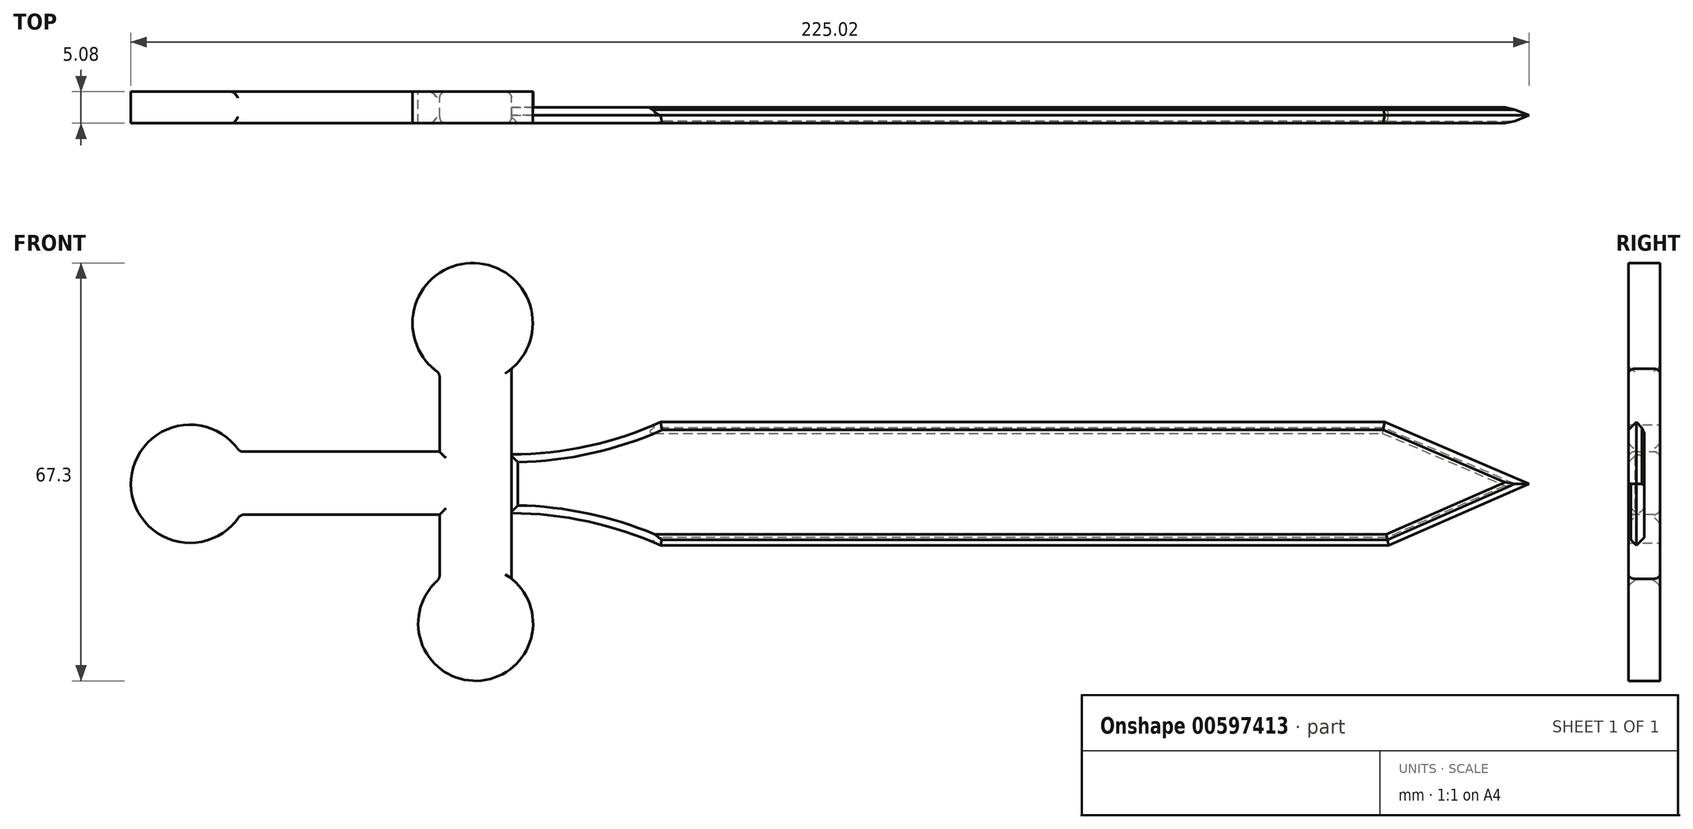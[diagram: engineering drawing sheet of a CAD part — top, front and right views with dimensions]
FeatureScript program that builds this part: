
annotation { "Feature Type Name" : "Feature", "Feature Type Description" : "" }
export const myFeature = defineFeature(function(context is Context, id is Id, definition is map)
    precondition{}
    {
        {
            var Q0;
            Q0=qCreatedBy(makeId("Front.planeOp"),FACE);
            var sketch = newSketch(context, id + "F0", { "sketchPlane" : qUnion([Q0])});
            skLineSegment(sketch, "E0.bottom", {"start": v(-78.76, 5.18) * mm, "end": v(-27.96, 5.18) * mm});
            skLineSegment(sketch, "E0.top", {"start": v(-78.76, -4.98) * mm, "end": v(-27.96, -4.98) * mm});
            skLineSegment(sketch, "E0.left", {"start": v(-78.76, 5.18) * mm, "end": v(-78.76, -4.98) * mm});
            skLineSegment(sketch, "E0.right", {"start": v(-27.96, 5.18) * mm, "end": v(-27.96, -4.98) * mm});
            skCircle(sketch, "E1", {"center": v(-75.72, 0) * mm, "radius": 9.52 * mm});
            skLineSegment(sketch, "E2.bottom", {"start": v(-35.56, 22.01) * mm, "end": v(-23.95, 22.01) * mm});
            skLineSegment(sketch, "E2.top", {"start": v(-35.56, -22.5) * mm, "end": v(-23.95, -22.5) * mm});
            skLineSegment(sketch, "E2.left", {"start": v(-35.56, 22.01) * mm, "end": v(-35.56, -22.5) * mm});
            skLineSegment(sketch, "E2.right", {"start": v(-23.95, 22.01) * mm, "end": v(-23.95, -22.5) * mm});
            skCircle(sketch, "E3", {"center": v(-30.24, 25.88) * mm, "radius": 9.68 * mm});
            skCircle(sketch, "E4", {"center": v(-29.75, -22.5) * mm, "radius": 9.24 * mm});
            skSolve(sketch);
        }
        {
            var Q0;
            Q0 = qSketchRegion(id + "F0", true);
            extrude(context, id + "F1", {"entities" : qUnion([Q0]), "endBound" : BoundingType.SYMMETRIC, "depth" : 5.08 * mm, "offsetDistance" : 25.4 * mm});
        }
        {
            var Q0;
            {var subQ0=sQuery(id+"F0.wireOp",EDGE,"E0.top");Q0=makeQuery(id+"F1.opExtrude","CAP_EDGE",EDGE,{"disambiguationData":[OSD([subQ0]),TDD([makeQuery(id+"F0.imprint","IMPRINT",EDGE,{"disambiguationData":[TD([[makeQuery(id+"F0.imprint","INTERSECT",VERTEX,{"derivedFrom":[subQ0,sQuery(id+"F0.wireOp",EDGE,"E1")]}),-1.0]])],"derivedFrom":subQ0})])],"isStart":false});}
            var Q1;
            {var subQ0=sQuery(id+"F0.wireOp",EDGE,"E0.bottom");Q1=makeQuery(id+"F1.opExtrude","CAP_EDGE",EDGE,{"disambiguationData":[OSD([subQ0]),TDD([makeQuery(id+"F0.imprint","IMPRINT",EDGE,{"disambiguationData":[TD([[makeQuery(id+"F0.imprint","INTERSECT",VERTEX,{"derivedFrom":[subQ0,sQuery(id+"F0.wireOp",EDGE,"E1")]}),-1.0]])],"derivedFrom":subQ0})])],"isStart":false});}
            var Q2;
            Q2=makeQuery(id+"F1.opExtrude","SWEPT_EDGE",EDGE,{"disambiguationData":[OSD([sQuery(id+"F0.wireOp",EDGE,"E0.top"),sQuery(id+"F0.wireOp",EDGE,"E1")])]});
            var Q3;
            Q3=makeQuery(id+"F1.opExtrude","SWEPT_EDGE",EDGE,{"disambiguationData":[OSD([sQuery(id+"F0.wireOp",EDGE,"E0.bottom"),sQuery(id+"F0.wireOp",EDGE,"E1")])]});
            var Q4;
            {var subQ0=sQuery(id+"F0.wireOp",EDGE,"E2.left");Q4=makeQuery(id+"F1.opExtrude","CAP_EDGE",EDGE,{"disambiguationData":[OSD([subQ0]),TDD([makeQuery(id+"F0.imprint","IMPRINT",EDGE,{"disambiguationData":[TD([[makeQuery(id+"F0.imprint","INTERSECT",VERTEX,{"derivedFrom":[sQuery(id+"F0.wireOp",EDGE,"E0.bottom"),subQ0]}),1.0]])],"derivedFrom":subQ0})])],"isStart":false});}
            var Q5;
            {var subQ0=sQuery(id+"F0.wireOp",EDGE,"E2.right");Q5=makeQuery(id+"F1.opExtrude","CAP_EDGE",EDGE,{"disambiguationData":[OSD([subQ0]),TDD([makeQuery(id+"F0.imprint","IMPRINT",EDGE,{"disambiguationData":[TD([[makeQuery(id+"F0.imprint","INTERSECT",VERTEX,{"derivedFrom":[sQuery(id+"F0.wireOp",EDGE,"E0.top"),subQ0]}),-1.0]])],"derivedFrom":subQ0})])],"isStart":false});}
            var Q6;
            {var subQ0=sQuery(id+"F0.wireOp",EDGE,"E2.right");Q6=makeQuery(id+"F1.opExtrude","CAP_EDGE",EDGE,{"disambiguationData":[OSD([subQ0]),TDD([makeQuery(id+"F0.imprint","IMPRINT",EDGE,{"disambiguationData":[TD([[makeQuery(id+"F0.imprint","INTERSECT",VERTEX,{"derivedFrom":[sQuery(id+"F0.wireOp",EDGE,"E0.bottom"),subQ0]}),1.0]])],"derivedFrom":subQ0})])],"isStart":false});}
            var Q7;
            {var subQ0=sQuery(id+"F0.wireOp",EDGE,"E2.left");Q7=makeQuery(id+"F1.opExtrude","CAP_EDGE",EDGE,{"disambiguationData":[OSD([subQ0]),TDD([makeQuery(id+"F0.imprint","IMPRINT",EDGE,{"disambiguationData":[TD([[makeQuery(id+"F0.imprint","INTERSECT",VERTEX,{"derivedFrom":[sQuery(id+"F0.wireOp",EDGE,"E0.top"),subQ0]}),-1.0]])],"derivedFrom":subQ0})])],"isStart":false});}
            var Q8;
            Q8=makeQuery(id+"F1.opExtrude","SWEPT_EDGE",EDGE,{"disambiguationData":[OSD([sQuery(id+"F0.wireOp",EDGE,"E2.left"),sQuery(id+"F0.wireOp",EDGE,"E3")])]});
            var Q9;
            Q9=makeQuery(id+"F1.opExtrude","SWEPT_EDGE",EDGE,{"disambiguationData":[OSD([sQuery(id+"F0.wireOp",EDGE,"E2.left"),sQuery(id+"F0.wireOp",EDGE,"E4")])]});
            var Q10;
            Q10=makeQuery(id+"F1.opExtrude","CAP_EDGE",EDGE,{"disambiguationData":[OSD([sQuery(id+"F0.wireOp",EDGE,"E0.bottom")])],"isStart":true});
            var Q11;
            Q11=makeQuery(id+"F1.opExtrude","CAP_EDGE",EDGE,{"disambiguationData":[OSD([sQuery(id+"F0.wireOp",EDGE,"E0.top")])],"isStart":true});
            var Q12;
            {var subQ0=sQuery(id+"F0.wireOp",EDGE,"E2.left");Q12=makeQuery(id+"F1.opExtrude","CAP_EDGE",EDGE,{"disambiguationData":[OSD([subQ0]),TDD([makeQuery(id+"F0.imprint","IMPRINT",EDGE,{"disambiguationData":[TD([[makeQuery(id+"F0.imprint","INTERSECT",VERTEX,{"derivedFrom":[sQuery(id+"F0.wireOp",EDGE,"E0.top"),subQ0]}),-1.0]])],"derivedFrom":subQ0})])],"isStart":true});}
            var Q13;
            {var subQ0=sQuery(id+"F0.wireOp",EDGE,"E2.right");Q13=makeQuery(id+"F1.opExtrude","CAP_EDGE",EDGE,{"disambiguationData":[OSD([subQ0]),TDD([makeQuery(id+"F0.imprint","IMPRINT",EDGE,{"disambiguationData":[TD([[makeQuery(id+"F0.imprint","INTERSECT",VERTEX,{"derivedFrom":[subQ0,sQuery(id+"F0.wireOp",EDGE,"CYwJg3hl-RuJJ-tjd6-eNec-YJv9DW7DHuWa")]}),-1.0]])],"derivedFrom":subQ0})])],"isStart":true});}
            var Q14;
            {var subQ0=sQuery(id+"F0.wireOp",EDGE,"E2.right");Q14=makeQuery(id+"F1.opExtrude","CAP_EDGE",EDGE,{"disambiguationData":[OSD([subQ0]),TDD([makeQuery(id+"F0.imprint","IMPRINT",EDGE,{"disambiguationData":[TD([[makeQuery(id+"F0.imprint","INTERSECT",VERTEX,{"derivedFrom":[subQ0,sQuery(id+"F0.wireOp",EDGE,"E3")]}),-1.0]])],"derivedFrom":subQ0})])],"isStart":true});}
            var Q15;
            {var subQ0=sQuery(id+"F0.wireOp",EDGE,"E2.left");Q15=makeQuery(id+"F1.opExtrude","CAP_EDGE",EDGE,{"disambiguationData":[OSD([subQ0]),TDD([makeQuery(id+"F0.imprint","IMPRINT",EDGE,{"disambiguationData":[TD([[makeQuery(id+"F0.imprint","INTERSECT",VERTEX,{"derivedFrom":[sQuery(id+"F0.wireOp",EDGE,"E0.bottom"),subQ0]}),1.0]])],"derivedFrom":subQ0})])],"isStart":true});}
            fillet(context, id + "F2", {"entities" : qUnion([Q0, Q1, Q2, Q3, Q4, Q5, Q6, Q7, Q8, Q9, Q10, Q11, Q12, Q13, Q14, Q15]), "radius" : 1.02 * mm, "tangentPropagation" : true, "allowEdgeOverflow" : false});
        }
        {
            var Q0;
            Q0=qCreatedBy(makeId("Front.planeOp"),FACE);
            var sketch = newSketch(context, id + "F3", { "sketchPlane" : qUnion([Q0])});
            skLineSegment(sketch, "E5", {"start": v(-24.21, 4.73) * mm, "end": v(-24.21, -4.73) * mm});
            skLineSegment(sketch, "E6", {"start": v(0, 9.92) * mm, "end": v(0, -9.92) * mm});
            skLineSegment(sketch, "E7.bottom", {"start": v(-24.21, 4.73) * mm, "end": v(0, 4.73) * mm});
            skLineSegment(sketch, "E7.top", {"start": v(-24.21, -4.73) * mm, "end": v(0, -4.73) * mm});
            skLineSegment(sketch, "E7.right", {"start": v(0, 4.73) * mm, "end": v(0, -4.73) * mm});
            skArc(sketch, "E8", {"start": v(-24.21, 4.73) * mm, "mid": v(-11.83, 6.05) * mm, "end": v(0, 9.92) * mm});
            skArc(sketch, "E9", {"start": v(0, -9.92) * mm, "mid": v(-11.83, -6.05) * mm, "end": v(-24.21, -4.73) * mm});
            skLineSegment(sketch, "E10", {"start": v(0, 9.92) * mm, "end": v(116.57, 9.92) * mm});
            skLineSegment(sketch, "E11", {"start": v(0, -9.92) * mm, "end": v(117.18, -9.92) * mm});
            skLineSegment(sketch, "E12", {"start": v(116.57, 9.92) * mm, "end": v(139.78, 0) * mm});
            skLineSegment(sketch, "E13", {"start": v(139.78, 0) * mm, "end": v(117.18, -9.92) * mm});
            skLineSegment(sketch, "E14", {"start": v(-24.21, -4.73) * mm, "end": v(-24.21, 4.73) * mm});
            skSolve(sketch);
        }
        {
            var Q0;
            Q0 = qSketchRegion(id + "F3", true);
            extrude(context, id + "F4", {"entities" : qUnion([Q0]), "operationType" : NewBodyOperationType.ADD, "depth" : 2.54 * mm, "offsetDistance" : 25.4 * mm});
        }
        {
            var Q0;
            Q0=makeQuery(id+"F4.opExtrude","CAP_FACE",FACE,{"disambiguationData":[OSD([sQuery(id+"F3.wireOp",EDGE,"E8"),sQuery(id+"F3.wireOp",EDGE,"E9"),sQuery(id+"F3.wireOp",EDGE,"E10"),sQuery(id+"F3.wireOp",EDGE,"E11"),sQuery(id+"F3.wireOp",EDGE,"E12"),sQuery(id+"F3.wireOp",EDGE,"E13"),sQuery(id+"F3.wireOp",EDGE,"E14")])],"isStart":false});
            var Q1;
            Q1=makeQuery(id+"F4.opExtrude","CAP_EDGE",EDGE,{"disambiguationData":[OSD([sQuery(id+"F3.wireOp",EDGE,"E10")])],"isStart":true});
            var Q2;
            Q2=makeQuery(id+"F4.opExtrude","CAP_EDGE",EDGE,{"disambiguationData":[OSD([sQuery(id+"F3.wireOp",EDGE,"E12")])],"isStart":true});
            chamfer(context, id + "F5", {"entities" : qUnion([Q0, Q1, Q2]), "width" : 1.27 * mm, "tangentPropagation" : true});
        }
        {
            var Q0;
            {var subQ0=sQuery(id+"F3.wireOp",EDGE,"E10");Q0=makeQuery(id+"F5.opChamfer","BLEND_EDGE",EDGE,{"blendedFrom":[makeQuery(id+"F4.opExtrude","CAP_EDGE",EDGE,{"disambiguationData":[OSD([subQ0])],"isStart":true}),makeQuery(id+"F4.opExtrude","CAP_FACE",FACE,{"disambiguationData":[OSD([sQuery(id+"F3.wireOp",EDGE,"E8"),sQuery(id+"F3.wireOp",EDGE,"E9"),subQ0,sQuery(id+"F3.wireOp",EDGE,"E11"),sQuery(id+"F3.wireOp",EDGE,"E12"),sQuery(id+"F3.wireOp",EDGE,"E13"),sQuery(id+"F3.wireOp",EDGE,"E14")])],"isStart":true})],"blendedInto":[makeQuery(id+"F4.opExtrude","CAP_FACE",FACE,{"disambiguationData":[OSD([sQuery(id+"F3.wireOp",EDGE,"E8"),sQuery(id+"F3.wireOp",EDGE,"E9"),subQ0,sQuery(id+"F3.wireOp",EDGE,"E11"),sQuery(id+"F3.wireOp",EDGE,"E12"),sQuery(id+"F3.wireOp",EDGE,"E13"),sQuery(id+"F3.wireOp",EDGE,"E14")])],"isStart":true})]});}
            var Q1;
            {var subQ0=sQuery(id+"F3.wireOp",EDGE,"E12");Q1=makeQuery(id+"F5.opChamfer","BLEND_EDGE",EDGE,{"blendedFrom":[makeQuery(id+"F4.opExtrude","CAP_EDGE",EDGE,{"disambiguationData":[OSD([subQ0])],"isStart":true}),makeQuery(id+"F4.opExtrude","CAP_FACE",FACE,{"disambiguationData":[OSD([sQuery(id+"F3.wireOp",EDGE,"E8"),sQuery(id+"F3.wireOp",EDGE,"E9"),sQuery(id+"F3.wireOp",EDGE,"E10"),sQuery(id+"F3.wireOp",EDGE,"E11"),subQ0,sQuery(id+"F3.wireOp",EDGE,"E13"),sQuery(id+"F3.wireOp",EDGE,"E14")])],"isStart":true})],"blendedInto":[makeQuery(id+"F4.opExtrude","CAP_FACE",FACE,{"disambiguationData":[OSD([sQuery(id+"F3.wireOp",EDGE,"E8"),sQuery(id+"F3.wireOp",EDGE,"E9"),sQuery(id+"F3.wireOp",EDGE,"E10"),sQuery(id+"F3.wireOp",EDGE,"E11"),subQ0,sQuery(id+"F3.wireOp",EDGE,"E13"),sQuery(id+"F3.wireOp",EDGE,"E14")])],"isStart":true})]});}
            var Q2;
            Q2=makeQuery(id+"F4.opExtrude","CAP_EDGE",EDGE,{"disambiguationData":[OSD([sQuery(id+"F3.wireOp",EDGE,"E13")])],"isStart":true});
            var Q3;
            Q3=makeQuery(id+"F4.opExtrude","CAP_EDGE",EDGE,{"disambiguationData":[OSD([sQuery(id+"F3.wireOp",EDGE,"E11")])],"isStart":true});
            var Q4;
            {var subQ0=sQuery(id+"F3.wireOp",EDGE,"E11");Q4=makeQuery(id+"F5.opChamfer","BLEND_EDGE",EDGE,{"blendedFrom":[makeQuery(id+"F4.opExtrude","CAP_EDGE",EDGE,{"disambiguationData":[OSD([subQ0])],"isStart":false}),makeQuery(id+"F4.opExtrude","CAP_FACE",FACE,{"disambiguationData":[OSD([sQuery(id+"F3.wireOp",EDGE,"E8"),sQuery(id+"F3.wireOp",EDGE,"E9"),sQuery(id+"F3.wireOp",EDGE,"E10"),subQ0,sQuery(id+"F3.wireOp",EDGE,"E12"),sQuery(id+"F3.wireOp",EDGE,"E13"),sQuery(id+"F3.wireOp",EDGE,"E14")])],"isStart":false})],"blendedInto":[makeQuery(id+"F4.opExtrude","CAP_FACE",FACE,{"disambiguationData":[OSD([sQuery(id+"F3.wireOp",EDGE,"E8"),sQuery(id+"F3.wireOp",EDGE,"E9"),sQuery(id+"F3.wireOp",EDGE,"E10"),subQ0,sQuery(id+"F3.wireOp",EDGE,"E12"),sQuery(id+"F3.wireOp",EDGE,"E13"),sQuery(id+"F3.wireOp",EDGE,"E14")])],"isStart":false})]});}
            var Q5;
            {var subQ0=sQuery(id+"F3.wireOp",EDGE,"E13");Q5=makeQuery(id+"F5.opChamfer","BLEND_EDGE",EDGE,{"blendedFrom":[makeQuery(id+"F4.opExtrude","CAP_EDGE",EDGE,{"disambiguationData":[OSD([subQ0])],"isStart":false}),makeQuery(id+"F4.opExtrude","CAP_FACE",FACE,{"disambiguationData":[OSD([sQuery(id+"F3.wireOp",EDGE,"E8"),sQuery(id+"F3.wireOp",EDGE,"E9"),sQuery(id+"F3.wireOp",EDGE,"E10"),sQuery(id+"F3.wireOp",EDGE,"E11"),sQuery(id+"F3.wireOp",EDGE,"E12"),subQ0,sQuery(id+"F3.wireOp",EDGE,"E14")])],"isStart":false})],"blendedInto":[makeQuery(id+"F4.opExtrude","CAP_FACE",FACE,{"disambiguationData":[OSD([sQuery(id+"F3.wireOp",EDGE,"E8"),sQuery(id+"F3.wireOp",EDGE,"E9"),sQuery(id+"F3.wireOp",EDGE,"E10"),sQuery(id+"F3.wireOp",EDGE,"E11"),sQuery(id+"F3.wireOp",EDGE,"E12"),subQ0,sQuery(id+"F3.wireOp",EDGE,"E14")])],"isStart":false})]});}
            chamfer(context, id + "F6", {"entities" : qUnion([Q0, Q1, Q2, Q3, Q4, Q5]), "width" : 1.27 * mm, "tangentPropagation" : true});
        }
        {
            var Q0;
            Q0=makeQuery(id+"F4.opExtrude","CAP_EDGE",EDGE,{"disambiguationData":[OSD([sQuery(id+"F3.wireOp",EDGE,"E8")])],"isStart":true});
            var Q1;
            Q1=makeQuery(id+"F4.opExtrude","CAP_EDGE",EDGE,{"disambiguationData":[OSD([sQuery(id+"F3.wireOp",EDGE,"E9")])],"isStart":true});
            fillet(context, id + "F7", {"entities" : qUnion([Q0, Q1]), "radius" : 1.27 * mm, "tangentPropagation" : true, "allowEdgeOverflow" : false});
        }
    });
